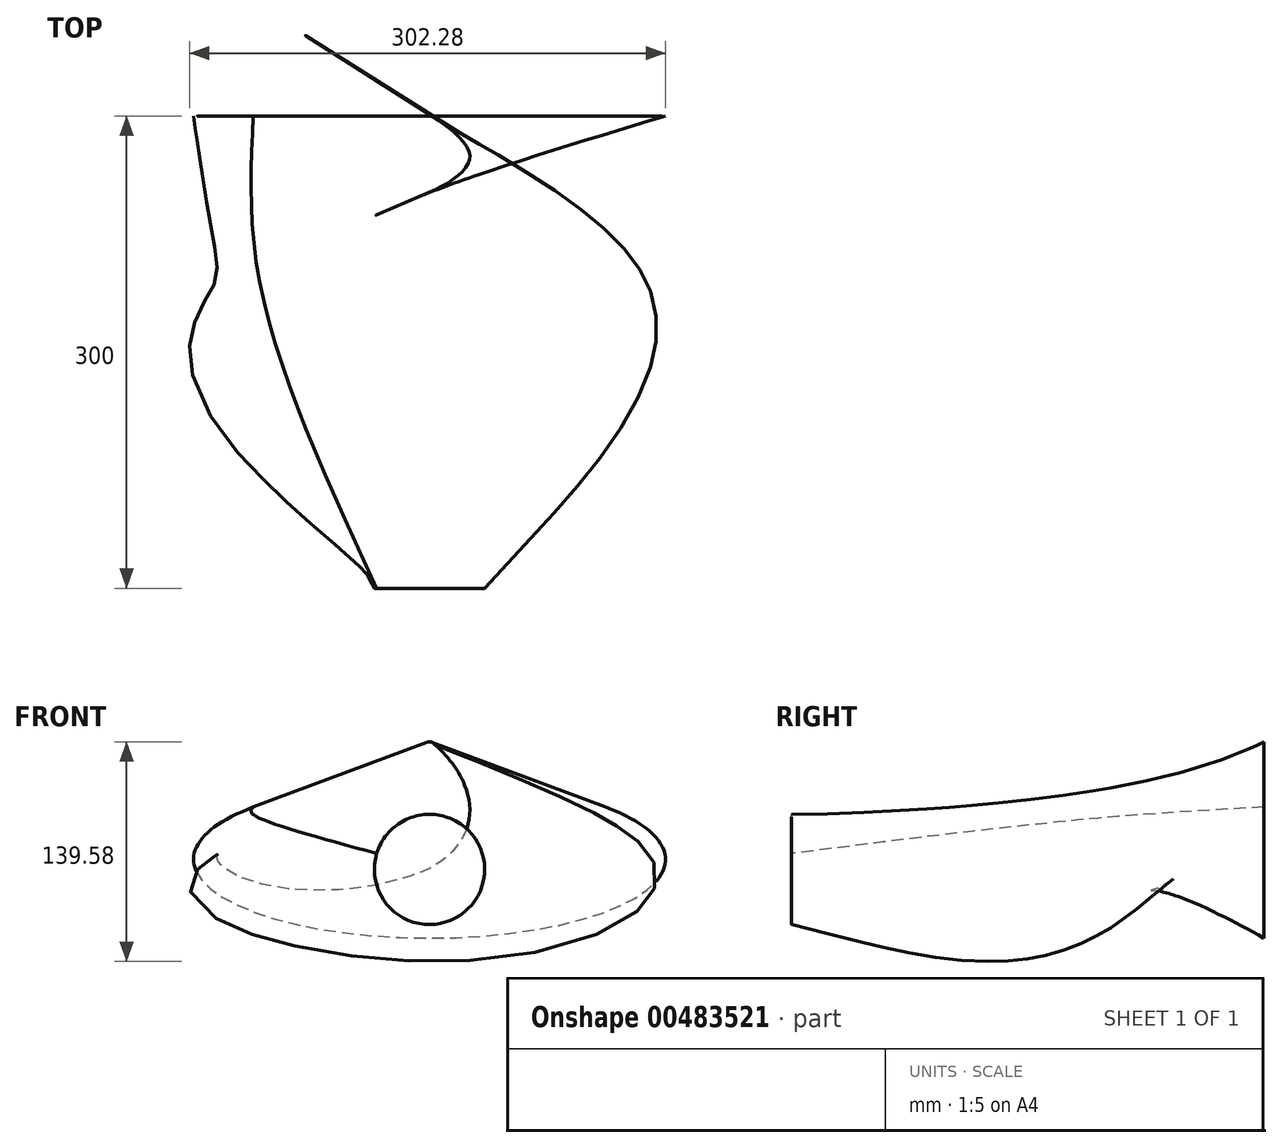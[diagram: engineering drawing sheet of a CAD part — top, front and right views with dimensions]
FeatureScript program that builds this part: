
annotation { "Feature Type Name" : "Feature", "Feature Type Description" : "" }
export const myFeature = defineFeature(function(context is Context, id is Id, definition is map)
    precondition{}
    {
        {
            var Q0;
            Q0=qCreatedBy(makeId("Front.planeOp"),FACE);
            var sketch = newSketch(context, id + "F0", { "sketchPlane" : qUnion([Q0])});
            skEllipticalArc(sketch, "E0", {});
            skLineSegment(sketch, "E1", {"start": v(-111.9, 33.25) * mm, "end": v(-1.75, 74.43) * mm});
            skLineSegment(sketch, "E2.MirrorCS", {"start": v(111.9, 33.25) * mm, "end": v(1.75, 74.43) * mm});
            skArc(sketch, "E3.filletArc", {"start": v(1.75, 74.43) * mm, "mid": v(0, 74.75) * mm, "end": v(-1.75, 74.43) * mm});
            const initialGuessF0  = {"E0": [0, 0, 1, 0, 0.14990906828316292, 0.04996224877510575, 2.4135316980658996, 0.7280609555238936]};
            skSetInitialGuess(sketch, initialGuessF0);
            skSolve(sketch);
        }
        {
            var Q0;
            Q0=qCreatedBy(makeId("Front.planeOp"),FACE);
            cPlane(context, id + "F1", {"entities" : qUnion([Q0]), "cplaneType" : CPlaneType.OFFSET, "offset" : 100 * mm, "width" : 150 * mm, "height" : 150 * mm});
        }
        {
            var Q0;
            Q0=qCreatedBy(id+"F1.planeOp",FACE);
            var sketch = newSketch(context, id + "F2", { "sketchPlane" : qUnion([Q0])});
            skEllipse(sketch, "E4", {"center": v(0, 0) * mm, "majorRadius": 135 * mm, "minorRadius": 45 * mm, "majorAxis": v(1, 0)});
            skSolve(sketch);
        }
        {
            var Q0;
            Q0=qCreatedBy(id+"F1.planeOp",FACE);
            cPlane(context, id + "F3", {"entities" : qUnion([Q0]), "cplaneType" : CPlaneType.OFFSET, "offset" : 200 * mm, "width" : 150 * mm, "height" : 150 * mm});
        }
        {
            var Q0;
            Q0=qCreatedBy(id+"F3.planeOp",FACE);
            var sketch = newSketch(context, id + "F4", { "sketchPlane" : qUnion([Q0])});
            skCircle(sketch, "E5", {"center": v(0, -6.33) * mm, "radius": 35 * mm});
            skSolve(sketch);
        }
        {
            var Q0;
            Q0=makeQuery(id+"F0.imprint","IMPRINT",FACE,{"disambiguationData":[TD([[makeQuery(id+"F0.imprint","IMPRINT",EDGE,{"derivedFrom":sQuery(id+"F0.wireOp",EDGE,"E0")}),1.0]])]});
            var Q1;
            Q1=makeQuery(id+"F2.imprint","IMPRINT",FACE,{"disambiguationData":[TD([[makeQuery(id+"F2.imprint","IMPRINT",EDGE,{"derivedFrom":sQuery(id+"F2.wireOp",EDGE,"E4")}),1.0]])]});
            var Q2;
            Q2=makeQuery(id+"F4.imprint","IMPRINT",FACE,{"disambiguationData":[TD([[makeQuery(id+"F4.imprint","IMPRINT",EDGE,{"derivedFrom":sQuery(id+"F4.wireOp",EDGE,"E5")}),1.0]])]});
            loft(context, id + "F5", {"sheetProfilesArray" : [{ "sheetProfileEntities" : qUnion([Q0]) }, { "sheetProfileEntities" : qUnion([Q1]) }, { "sheetProfileEntities" : qUnion([Q2]) }]});
        }
    });
